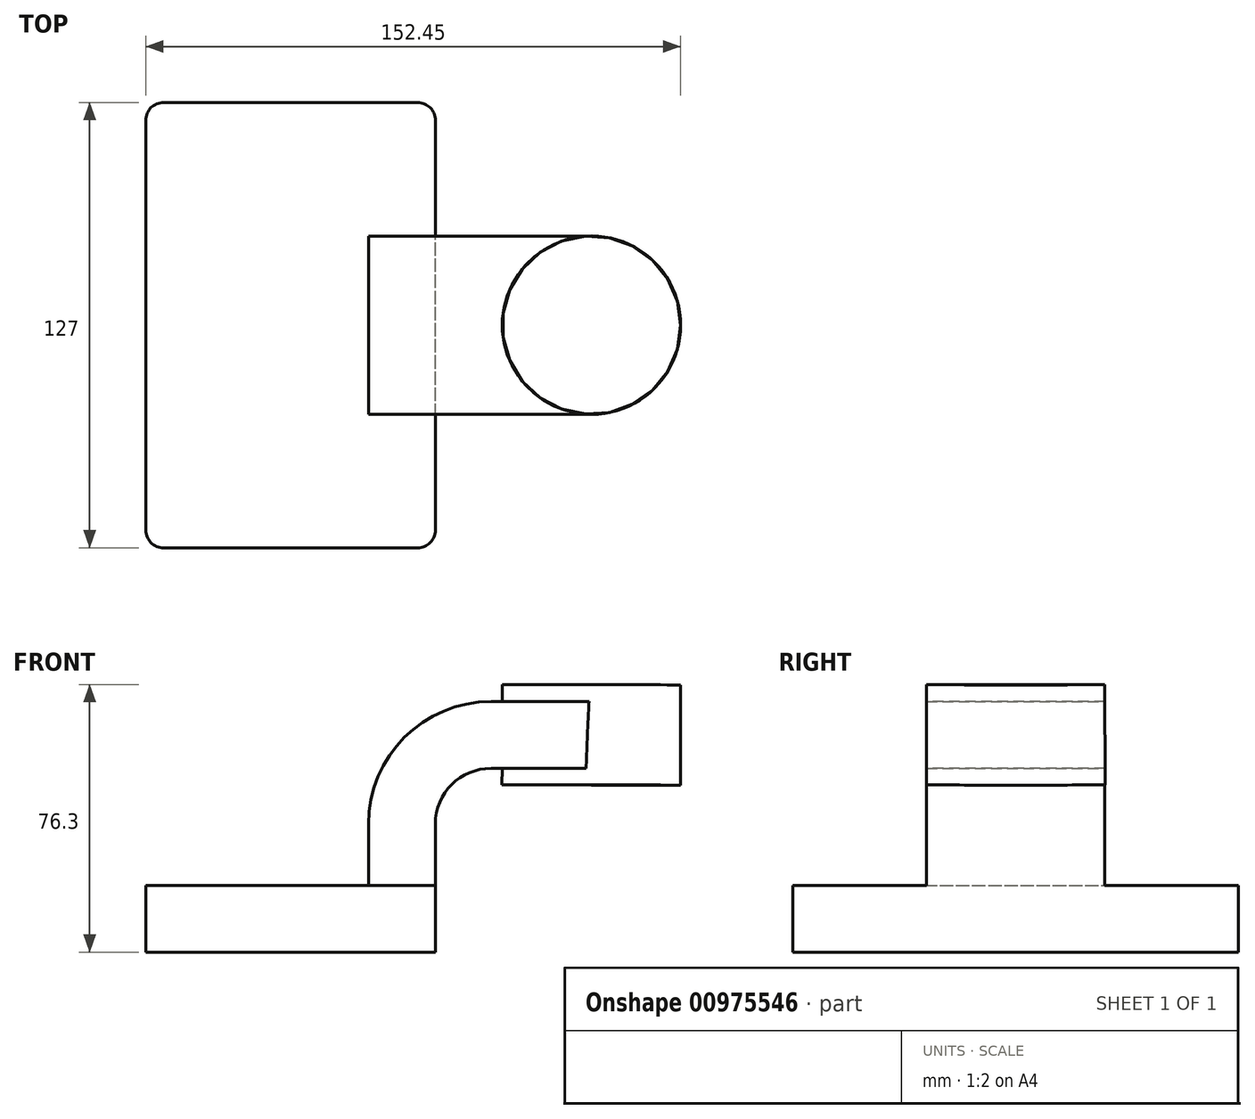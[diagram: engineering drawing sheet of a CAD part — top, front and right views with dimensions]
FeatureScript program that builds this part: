
annotation { "Feature Type Name" : "Feature", "Feature Type Description" : "" }
export const myFeature = defineFeature(function(context is Context, id is Id, definition is map)
    precondition{}
    {
        {
            var Q0;
            Q0=qCreatedBy(makeId("Front.planeOp"),FACE);
            var sketch = newSketch(context, id + "F0", { "sketchPlane" : qUnion([Q0])});
            skLineSegment(sketch, "E0.bottom", {"start": v(-41.28, 9.52) * mm, "end": v(41.27, 9.53) * mm});
            skLineSegment(sketch, "E0.top", {"start": v(-41.28, -9.53) * mm, "end": v(41.28, -9.53) * mm});
            skLineSegment(sketch, "E0.left", {"start": v(-41.28, 9.52) * mm, "end": v(-41.27, -9.53) * mm});
            skLineSegment(sketch, "E0.right", {"start": v(41.28, 9.53) * mm, "end": v(41.28, -9.52) * mm});
            skPoint(sketch, "E0.middle", {"position": v(0, 0) * mm});
            skLineSegment(sketch, "E1", {"start": v(41.27, 9.53) * mm, "end": v(41.27, 27) * mm});
            skLineSegment(sketch, "E2.bottom", {"start": v(111.18, 38.1) * mm, "end": v(60.38, 38.1) * mm});
            skLineSegment(sketch, "E2.top", {"start": v(111.18, 66.68) * mm, "end": v(60.38, 66.68) * mm});
            skLineSegment(sketch, "E2.left", {"start": v(111.18, 38.1) * mm, "end": v(111.18, 66.67) * mm});
            skLineSegment(sketch, "E2.right", {"start": v(60.38, 38.1) * mm, "end": v(60.38, 66.67) * mm});
            skPoint(sketch, "E2.middle", {"position": v(85.78, 52.39) * mm});
            skArc(sketch, "E3", {"start": v(41.27, 27) * mm, "mid": v(45.92, 38.23) * mm, "end": v(57.15, 42.88) * mm});
            skLineSegment(sketch, "E4", {"start": v(57.15, 42.88) * mm, "end": v(85.72, 42.88) * mm});
            skLineSegment(sketch, "E5.0", {"start": v(57.15, 61.93) * mm, "end": v(85.72, 61.93) * mm});
            skArc(sketch, "E5.1", {"start": v(22.22, 27) * mm, "mid": v(32.45, 51.7) * mm, "end": v(57.15, 61.93) * mm});
            skLineSegment(sketch, "E5.2", {"start": v(22.22, 9.53) * mm, "end": v(22.22, 27) * mm});
            skFitSpline(sketch, "E6", {"points": [v(-41.28, 9.52) * mm, v(57.15, 61.93) * mm], "startDerivative": vector(42.15, 125.63) * mm, "endDerivative": vector(120.25, -6.58) * mm});
            skLineSegment(sketch, "E7", {"start": v(85.72, 61.93) * mm, "end": v(85.72, 42.88) * mm});
            skLineSegment(sketch, "E8", {"start": v(85.78, 66.68) * mm, "end": v(85.72, 38.1) * mm});
            skSolve(sketch);
        }
        {
            var Q0;
            Q0=makeQuery(id+"F0.imprint","IMPRINT",FACE,{"disambiguationData":[TD([[makeQuery(id+"F0.imprint","IMPRINT",EDGE,{"derivedFrom":sQuery(id+"F0.wireOp",EDGE,"E0.top")}),1.0]])]});
            extrude(context, id + "F1", {"entities" : qUnion([Q0]), "endBound" : BoundingType.SYMMETRIC, "depth" : 127 * mm, "offsetDistance" : 25.4 * mm});
        }
        {
            var Q0;
            {var subQ6=sQuery(id+"F0.wireOp",EDGE,"E1");Q0=makeQuery(id+"F0.imprint","IMPRINT",FACE,{"disambiguationData":[TD([[makeQuery(id+"F0.imprint","IMPRINT",EDGE,{"derivedFrom":subQ6}),1.0]])]});}
            var Q1;
            {var subQ5=sQuery(id+"F0.wireOp",EDGE,"E7");Q1=makeQuery(id+"F0.imprint","IMPRINT",FACE,{"disambiguationData":[TD([[makeQuery(id+"F0.imprint","IMPRINT",EDGE,{"derivedFrom":subQ5}),-1.0]])]});}
            extrude(context, id + "F2", {"entities" : qUnion([Q0, Q1]), "operationType" : NewBodyOperationType.ADD, "endBound" : BoundingType.SYMMETRIC, "depth" : 50.8 * mm, "offsetDistance" : 25.4 * mm});
        }
        {
            var Q0;
            Q0=makeQuery(id+"F0.imprint","IMPRINT",FACE,{"disambiguationData":[TD([[makeQuery(id+"F0.imprint","IMPRINT",EDGE,{"derivedFrom":sQuery(id+"F0.wireOp",EDGE,"E5.1")}),1.0]])]});
            extrude(context, id + "F3", {"entities" : qUnion([Q0]), "operationType" : NewBodyOperationType.ADD, "endBound" : BoundingType.SYMMETRIC, "depth" : 25.4 * mm, "offsetDistance" : 25.4 * mm});
        }
        {
            var Q0;
            {var subQ0=sQuery(id+"F0.wireOp",EDGE,"E2.left");Q0=makeQuery(id+"F0.imprint","IMPRINT",FACE,{"disambiguationData":[TD([[makeQuery(id+"F0.imprint","IMPRINT",EDGE,{"derivedFrom":subQ0}),1.0]])]});}
            var Q1;
            Q1=sQuery(id+"F0.wireOp",EDGE,"E8");
            revolve(context, id + "F4", {"operationType" : NewBodyOperationType.ADD, "surfaceOperationType" : NewSurfaceOperationType.NEW, "entities" : qUnion([Q0]), "axis" : qUnion([Q1]), "revolveType" : RevolveType.FULL});
        }
        {
            var Q0;
            Q0=makeQuery(id+"F1.opExtrude","CAP_EDGE",EDGE,{"disambiguationData":[OSD([sQuery(id+"F0.wireOp",EDGE,"E0.left")])],"isStart":false});
            var Q1;
            Q1=makeQuery(id+"F1.opExtrude","CAP_EDGE",EDGE,{"disambiguationData":[OSD([sQuery(id+"F0.wireOp",EDGE,"E0.right")])],"isStart":false});
            var Q2;
            Q2=makeQuery(id+"F1.opExtrude","CAP_EDGE",EDGE,{"disambiguationData":[OSD([sQuery(id+"F0.wireOp",EDGE,"E0.right")])],"isStart":true});
            var Q3;
            Q3=makeQuery(id+"F1.opExtrude","CAP_EDGE",EDGE,{"disambiguationData":[OSD([sQuery(id+"F0.wireOp",EDGE,"E0.left")])],"isStart":true});
            fillet(context, id + "F5", {"entities" : qUnion([Q0, Q1, Q2, Q3]), "radius" : 5.08 * mm, "tangentPropagation" : true, "allowEdgeOverflow" : false});
        }
    });
